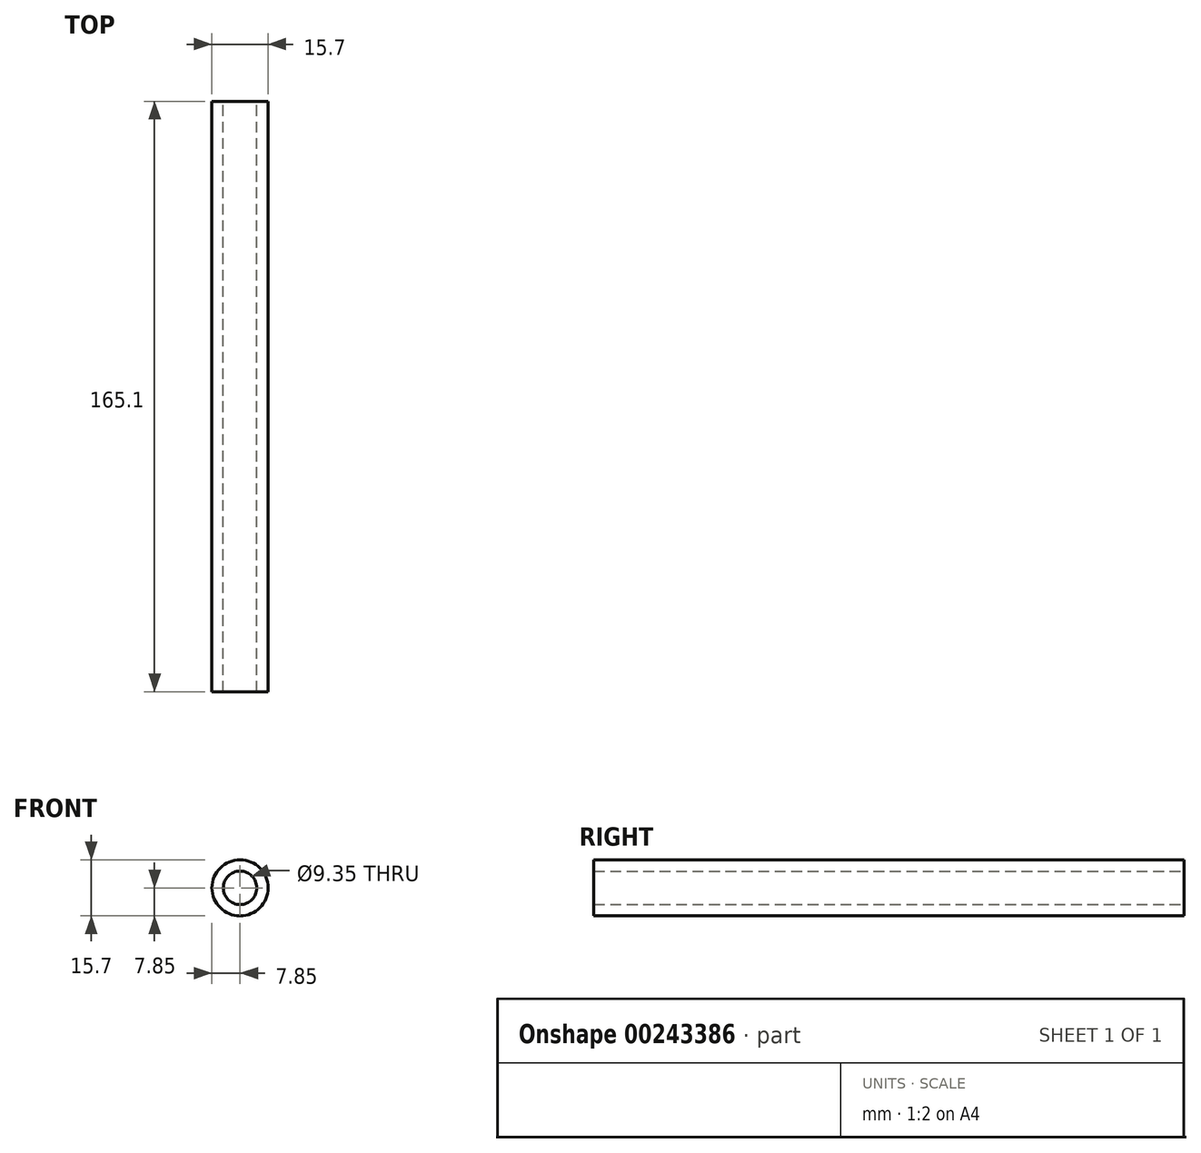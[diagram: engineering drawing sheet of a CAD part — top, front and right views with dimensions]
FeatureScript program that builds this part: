
annotation { "Feature Type Name" : "Feature", "Feature Type Description" : "" }
export const myFeature = defineFeature(function(context is Context, id is Id, definition is map)
    precondition{}
    {
        {
            var Q0;
            Q0=qCreatedBy(makeId("Front.planeOp"),FACE);
            var sketch = newSketch(context, id + "F0", { "sketchPlane" : qUnion([Q0])});
            skCircle(sketch, "E0", {"center": v(0, 0) * mm, "radius": 4.67 * mm});
            skCircle(sketch, "E1", {"center": v(0, 0) * mm, "radius": 7.85 * mm});
            skSolve(sketch);
        }
        {
            var Q0;
            Q0 = qSketchRegion(id + "F0", true);
            extrude(context, id + "F1", {"entities" : qUnion([Q0]), "depth" : 165.1 * mm});
        }
    });
